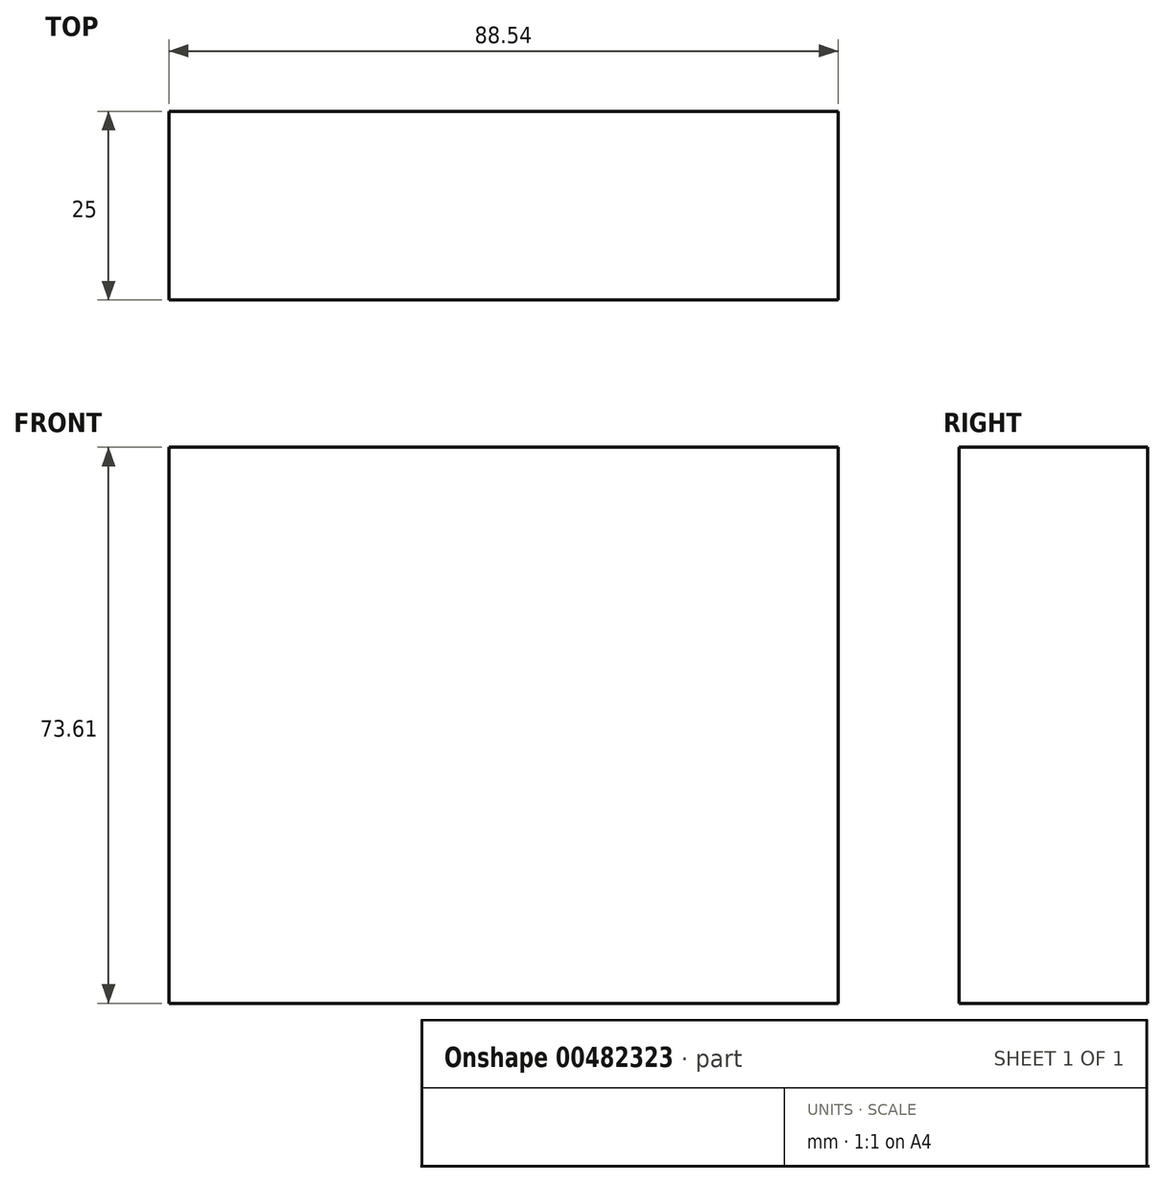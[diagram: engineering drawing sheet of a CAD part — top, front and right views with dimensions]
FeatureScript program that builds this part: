
annotation { "Feature Type Name" : "Feature", "Feature Type Description" : "" }
export const myFeature = defineFeature(function(context is Context, id is Id, definition is map)
    precondition{}
    {
        {
            var Q0;
            Q0=qCreatedBy(makeId("Front.planeOp"),FACE);
            var sketch = newSketch(context, id + "F0", { "sketchPlane" : qUnion([Q0])});
            skLineSegment(sketch, "E0.bottom", {"start": v(-44.27, 32.39) * mm, "end": v(44.27, 32.39) * mm});
            skLineSegment(sketch, "E0.top", {"start": v(-44.27, -41.22) * mm, "end": v(44.27, -41.22) * mm});
            skLineSegment(sketch, "E0.left", {"start": v(-44.27, 32.39) * mm, "end": v(-44.27, -41.22) * mm});
            skLineSegment(sketch, "E0.right", {"start": v(44.27, 32.39) * mm, "end": v(44.27, -41.22) * mm});
            skSolve(sketch);
        }
        {
            var Q0;
            Q0=makeQuery(id+"F0.imprint","IMPRINT",FACE,{"disambiguationData":[TD([[makeQuery(id+"F0.imprint","IMPRINT",EDGE,{"derivedFrom":sQuery(id+"F0.wireOp",EDGE,"E0.bottom")}),-1.0]])]});
            extrude(context, id + "F1", {"entities" : qUnion([Q0]), "depth" : 25 * mm});
        }
    });
